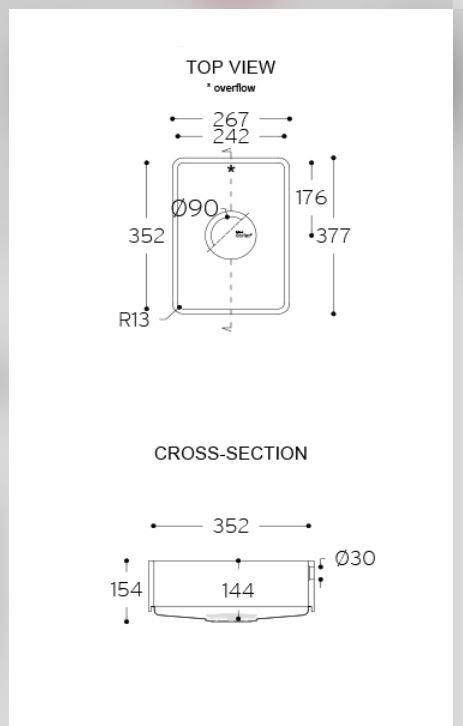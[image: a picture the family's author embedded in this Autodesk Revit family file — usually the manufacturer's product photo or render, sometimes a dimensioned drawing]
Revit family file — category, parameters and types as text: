
# Revit family: Sink-Corian-European-Sparkling-9502
name_source: partatom
category: Plumbing Fixtures
revit_build: Autodesk Revit 2015 (Build: 20140606_1530(x64)
units: mm (PartAtom-declared; Revit-internal decimal feet)

## types (1)
- 9502
    CWFU = 0
    Cost = 0 $
    Default Elevation = 1219 mm
    Depth = 154 mm  [stored 0.505249 ft]
    Description = Kitchen Sink Europe Specification
    Finish = Solid Surface Sink - DuPont - Bisque
    HWFU = 0
    Interior Length = 352 mm  [stored 1.15486 ft]
    Interior Width = 242 mm  [stored 0.793963 ft]
    Length = 377 mm  [stored 1.23688 ft]
    Manufacturer = DuPont
    Model = Sparkling 9502
    Product Page URL = http://www.corian.uk
    Sink Base = Metal - DuPont - Stainless Steel
    Sink Colors Available = Available in all the colours of Corian for kitchen worksurfaces
    URL = http://www.corian.uk
    Version = 2015 - v1.0b
    WFU = 0
    Width = 267 mm  [stored 0.875984 ft]

note: [stored X ft] marks values corroborated as IEEE doubles in the binary element streams (Revit-internal decimal feet)

## geometry (parser evidence)
native form markers: Sweep x4
no freeform markers — native parametric forms only
